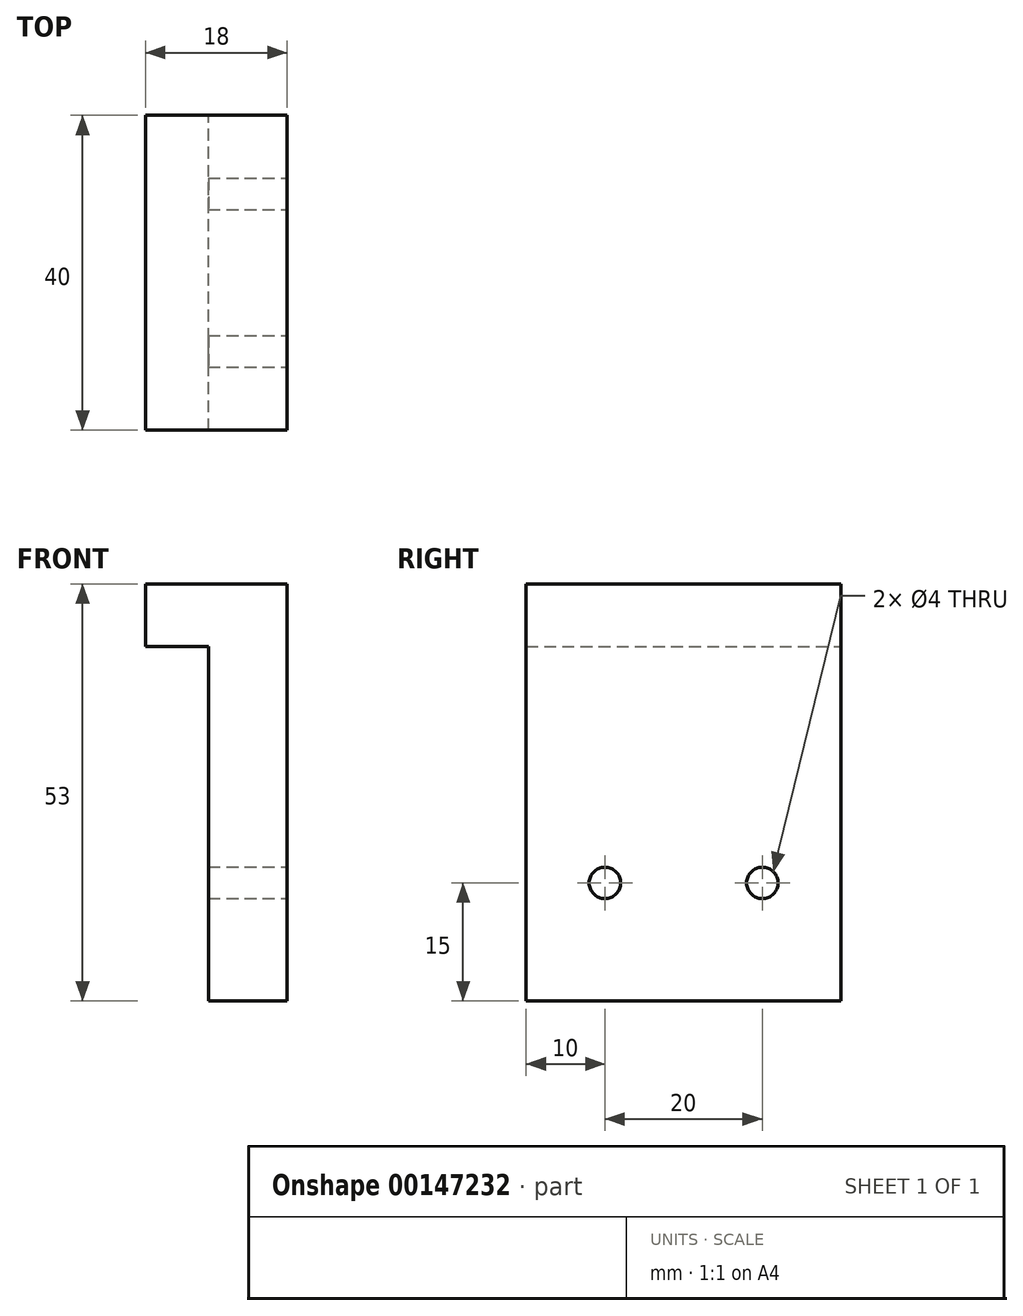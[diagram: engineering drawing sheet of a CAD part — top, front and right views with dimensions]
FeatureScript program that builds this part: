
annotation { "Feature Type Name" : "Feature", "Feature Type Description" : "" }
export const myFeature = defineFeature(function(context is Context, id is Id, definition is map)
    precondition{}
    {
        {
            var Q0;
            Q0=qCreatedBy(makeId("Front.planeOp"),FACE);
            var sketch = newSketch(context, id + "F0", { "sketchPlane" : qUnion([Q0])});
            skLineSegment(sketch, "E0", {"start": v(-10, 0) * mm, "end": v(0, 0) * mm});
            skLineSegment(sketch, "E1", {"start": v(0, 0) * mm, "end": v(0, 53) * mm});
            skLineSegment(sketch, "E2", {"start": v(0, 53) * mm, "end": v(-18, 53) * mm});
            skLineSegment(sketch, "E3", {"start": v(-18, 53) * mm, "end": v(-18, 45) * mm});
            skLineSegment(sketch, "E4", {"start": v(-18, 45) * mm, "end": v(-10, 45) * mm});
            skLineSegment(sketch, "E5", {"start": v(-10, 45) * mm, "end": v(-10, 0) * mm});
            skSolve(sketch);
        }
        {
            var Q0;
            Q0 = qSketchRegion(id + "F0", true);
            extrude(context, id + "F1", {"entities" : qUnion([Q0]), "endBound" : BoundingType.SYMMETRIC, "depth" : 40 * mm});
        }
        {
            var Q0;
            Q0=makeQuery(id+"F1.opExtrude","SWEPT_FACE",FACE,{"disambiguationData":[OSD([sQuery(id+"F0.wireOp",EDGE,"E1")])]});
            var sketch = newSketch(context, id + "F2", { "sketchPlane" : qUnion([Q0])});
            skCircle(sketch, "E6", {"center": v(-10, 15) * mm, "radius": 2 * mm});
            skCircle(sketch, "E7", {"center": v(10, 15) * mm, "radius": 2 * mm});
            skLineSegment(sketch, "E8", {"start": v(-10, 15) * mm, "end": v(10, 15) * mm, "construction": true});
            skLineSegment(sketch, "E9", {"start": v(0, 15) * mm, "end": v(0, 0) * mm, "construction": true});
            skSolve(sketch);
        }
        {
            var Q0;
            Q0 = qSketchRegion(id + "F2", true);
            extrude(context, id + "F3", {"entities" : qUnion([Q0]), "operationType" : NewBodyOperationType.REMOVE, "endBound" : BoundingType.THROUGH_ALL, "oppositeDirection" : true, "depth" : 25 * mm});
        }
    });
